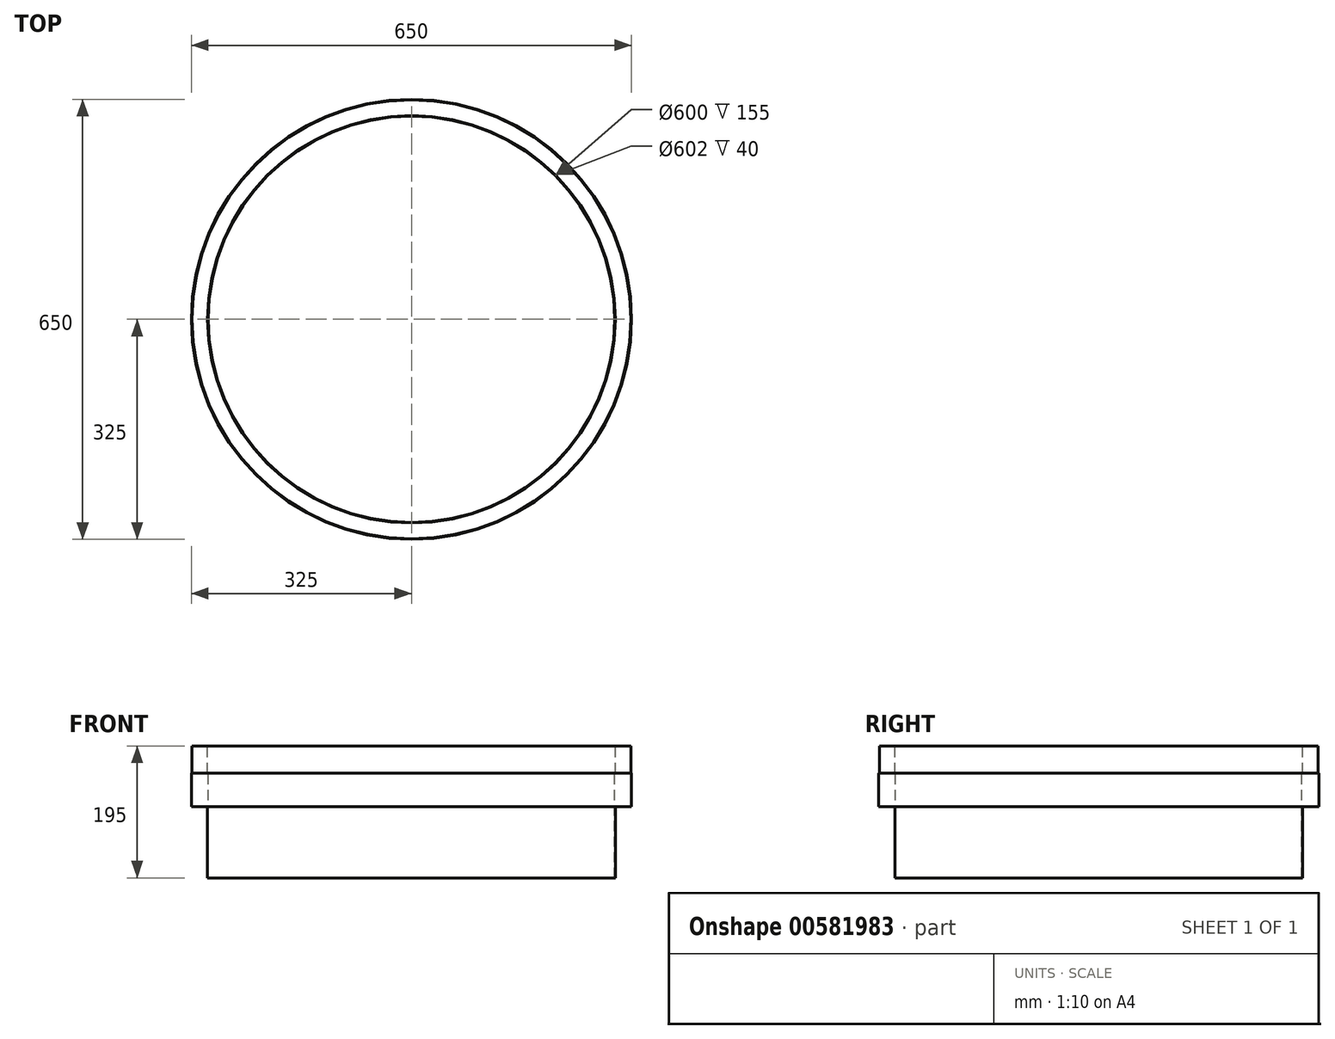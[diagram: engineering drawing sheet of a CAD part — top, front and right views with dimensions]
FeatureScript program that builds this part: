
annotation { "Feature Type Name" : "Feature", "Feature Type Description" : "" }
export const myFeature = defineFeature(function(context is Context, id is Id, definition is map)
    precondition{}
    {
        {
            var Q0;
            Q0=qCreatedBy(makeId("Front.planeOp"),FACE);
            var sketch = newSketch(context, id + "F0", { "sketchPlane" : qUnion([Q0])});
            skLineSegment(sketch, "E0", {"start": v(0, 710.75) * mm, "end": v(0, -704.58) * mm, "construction": true});
            skLineSegment(sketch, "E1", {"start": v(-300, 295.65) * mm, "end": v(-300, 410.65) * mm});
            skLineSegment(sketch, "E2", {"start": v(-300, 410.65) * mm, "end": v(-301, 410.65) * mm});
            skLineSegment(sketch, "E3", {"start": v(-324, 410.65) * mm, "end": v(-325, 410.65) * mm});
            skLineSegment(sketch, "E4", {"start": v(-325, 410.65) * mm, "end": v(-325, 360.65) * mm});
            skLineSegment(sketch, "E5", {"start": v(-325, 360.65) * mm, "end": v(-301, 360.65) * mm});
            skLineSegment(sketch, "E6", {"start": v(-301, 360.65) * mm, "end": v(-301, 295.65) * mm});
            skLineSegment(sketch, "E7", {"start": v(-324, 450.65) * mm, "end": v(-324, 410.65) * mm});
            skLineSegment(sketch, "E8", {"start": v(-324, 450.65) * mm, "end": v(-301, 450.65) * mm});
            skLineSegment(sketch, "E9", {"start": v(-301, 410.65) * mm, "end": v(-301, 450.65) * mm});
            skLineSegment(sketch, "E10", {"start": v(-300, 295.65) * mm, "end": v(-300, 255.65) * mm});
            skLineSegment(sketch, "E11", {"start": v(-301, 295.65) * mm, "end": v(-301, 255.65) * mm});
            skLineSegment(sketch, "E12", {"start": v(-301, 255.65) * mm, "end": v(-300, 255.65) * mm});
            skSolve(sketch);
        }
        {
            var Q0;
            Q0=qSketchRegion(id+"F0",true);
            var Q1;
            Q1=sQuery(id+"F0.wireOp",EDGE,"E0");
            revolve(context, id + "F1", {"entities" : qUnion([Q0]), "axis" : qUnion([Q1]), "revolveType" : RevolveType.FULL});
        }
    });
